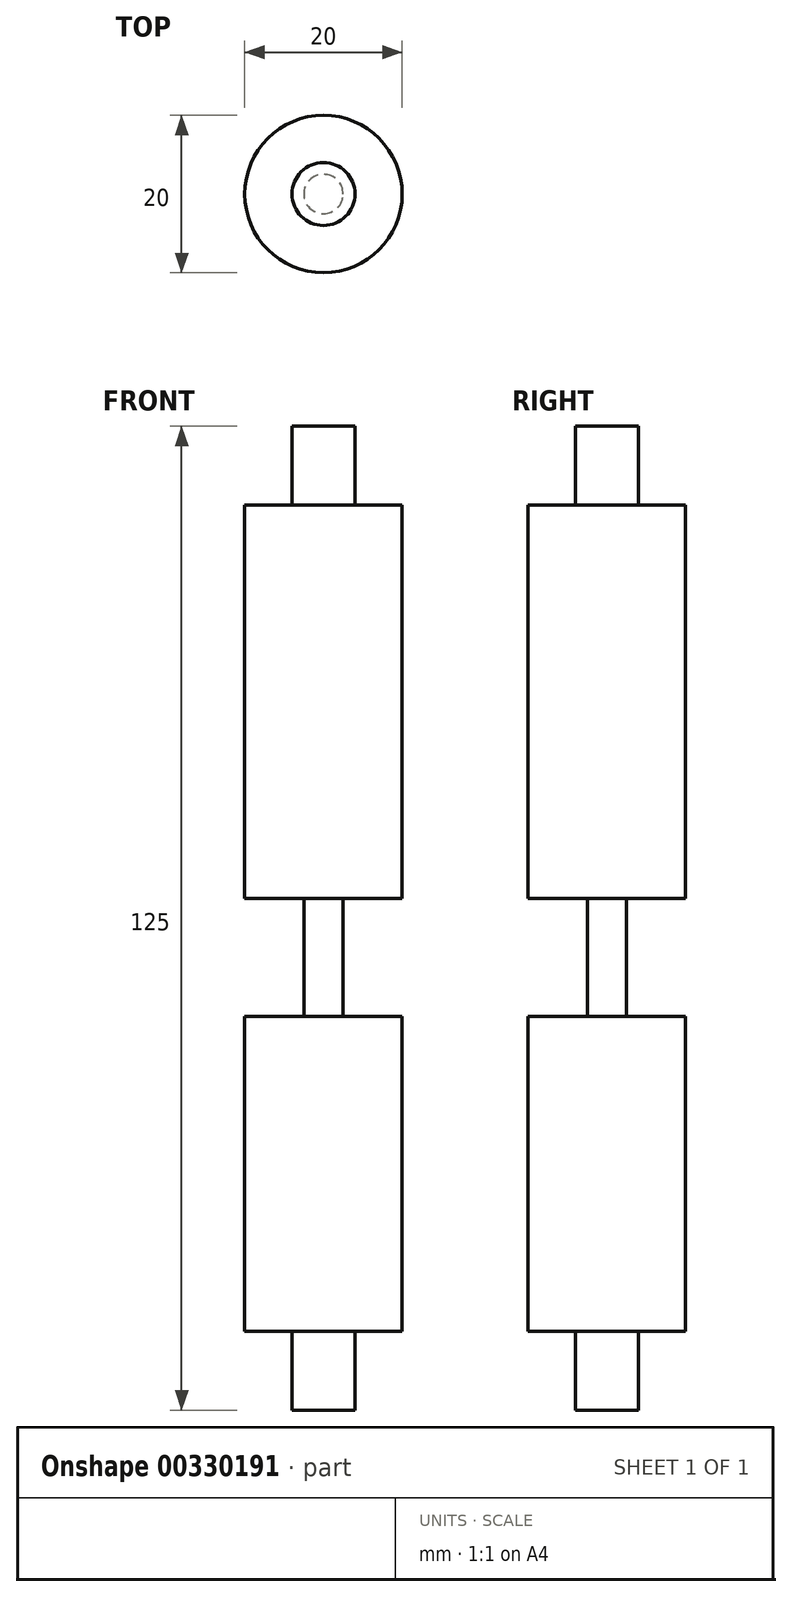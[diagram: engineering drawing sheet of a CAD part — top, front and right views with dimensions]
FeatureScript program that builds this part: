
annotation { "Feature Type Name" : "Feature", "Feature Type Description" : "" }
export const myFeature = defineFeature(function(context is Context, id is Id, definition is map)
    precondition{}
    {
        {
            var Q0;
            Q0=qCreatedBy(makeId("Front.planeOp"),FACE);
            var sketch = newSketch(context, id + "F0", { "sketchPlane" : qUnion([Q0])});
            skLineSegment(sketch, "E0", {"start": v(-2.5, 0) * mm, "end": v(-2.5, 7.5) * mm});
            skLineSegment(sketch, "E1", {"start": v(-2.5, 7.5) * mm, "end": v(-10, 7.5) * mm});
            skLineSegment(sketch, "E2", {"start": v(-10, 7.5) * mm, "end": v(-10, 57.5) * mm});
            skLineSegment(sketch, "E3", {"start": v(-10, 57.5) * mm, "end": v(-4, 57.5) * mm});
            skLineSegment(sketch, "E4", {"start": v(-4, 57.5) * mm, "end": v(-4, 67.5) * mm});
            skLineSegment(sketch, "E5", {"start": v(-4, 67.5) * mm, "end": v(0, 67.5) * mm});
            skLineSegment(sketch, "E6", {"start": v(0, 67.5) * mm, "end": v(0, 0) * mm});
            skLineSegment(sketch, "E7", {"start": v(-2.5, 0) * mm, "end": v(-2.5, -7.5) * mm});
            skLineSegment(sketch, "E8", {"start": v(-2.5, -7.5) * mm, "end": v(-10, -7.5) * mm});
            skLineSegment(sketch, "E9", {"start": v(-10, -7.5) * mm, "end": v(-10, -47.5) * mm});
            skLineSegment(sketch, "E10", {"start": v(-10, -47.5) * mm, "end": v(-4, -47.5) * mm});
            skLineSegment(sketch, "E11", {"start": v(-4, -47.5) * mm, "end": v(-4, -57.5) * mm});
            skLineSegment(sketch, "E12", {"start": v(-4, -57.5) * mm, "end": v(0, -57.5) * mm});
            skLineSegment(sketch, "E13", {"start": v(0, -57.5) * mm, "end": v(0, 0) * mm});
            skSolve(sketch);
        }
        {
            var Q0;
            Q0=makeQuery(id+"F0.imprint","IMPRINT",FACE,{"disambiguationData":[TD([[makeQuery(id+"F0.imprint","IMPRINT",EDGE,{"derivedFrom":sQuery(id+"F0.wireOp",EDGE,"E0")}),-1.0]])]});
            var Q1;
            Q1=sQuery(id+"F0.wireOp",EDGE,"E6");
            revolve(context, id + "F1", {"entities" : qUnion([Q0]), "axis" : qUnion([Q1]), "revolveType" : RevolveType.FULL});
        }
    });
